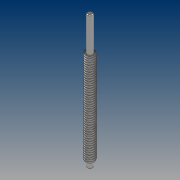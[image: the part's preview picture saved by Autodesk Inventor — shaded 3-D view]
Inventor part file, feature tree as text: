
AUTODESK INVENTOR PART (.ipt)
format: ipt  version: 2021 (Build 250183000, 183)  size: 612,352 bytes
history: native  units: mm
features: sketch x2, revolve x1, helix x1, chamfer x1, projected_geometry x1
ambient origin geometry x8: Origin, YZ Plane, XZ Plane, XY Plane, X Axis, Y Axis, Z Axis, Center Point
bodies: Solid1 (feature_tree)
feature tree (6):
  revolve  "Revolution1"  [1 undecoded]
  helix  "Coil1"  [1 undecoded]
  chamfer  "Chamfer1"  Distance=200.0mm
  sketch  "Sketch1"  dims[d0=9.0mm d1=4.0mm d2=6.0mm]
  sketch  "Sketch2"  dims[d3=52.0mm d4=200.0mm d5=90.0deg d6=1.0mm d7=12.217305mm d8=1.0mm d9=139.0mm d10=3.0mm d11=139.0mm d12=10.0mm d13=0.0mm d14=90.0deg d15=90.0deg d16=0.0mm d17=0.0mm d18=1.0mm d19=2.0mm d20=45.0deg]
  projected_geometry  "Projected Loop1"
note: 2 required parameter values undecoded (feature->parameter linkage not recoverable at this tier; creation-order binding heuristic only, values carry confidence <= 0.55)